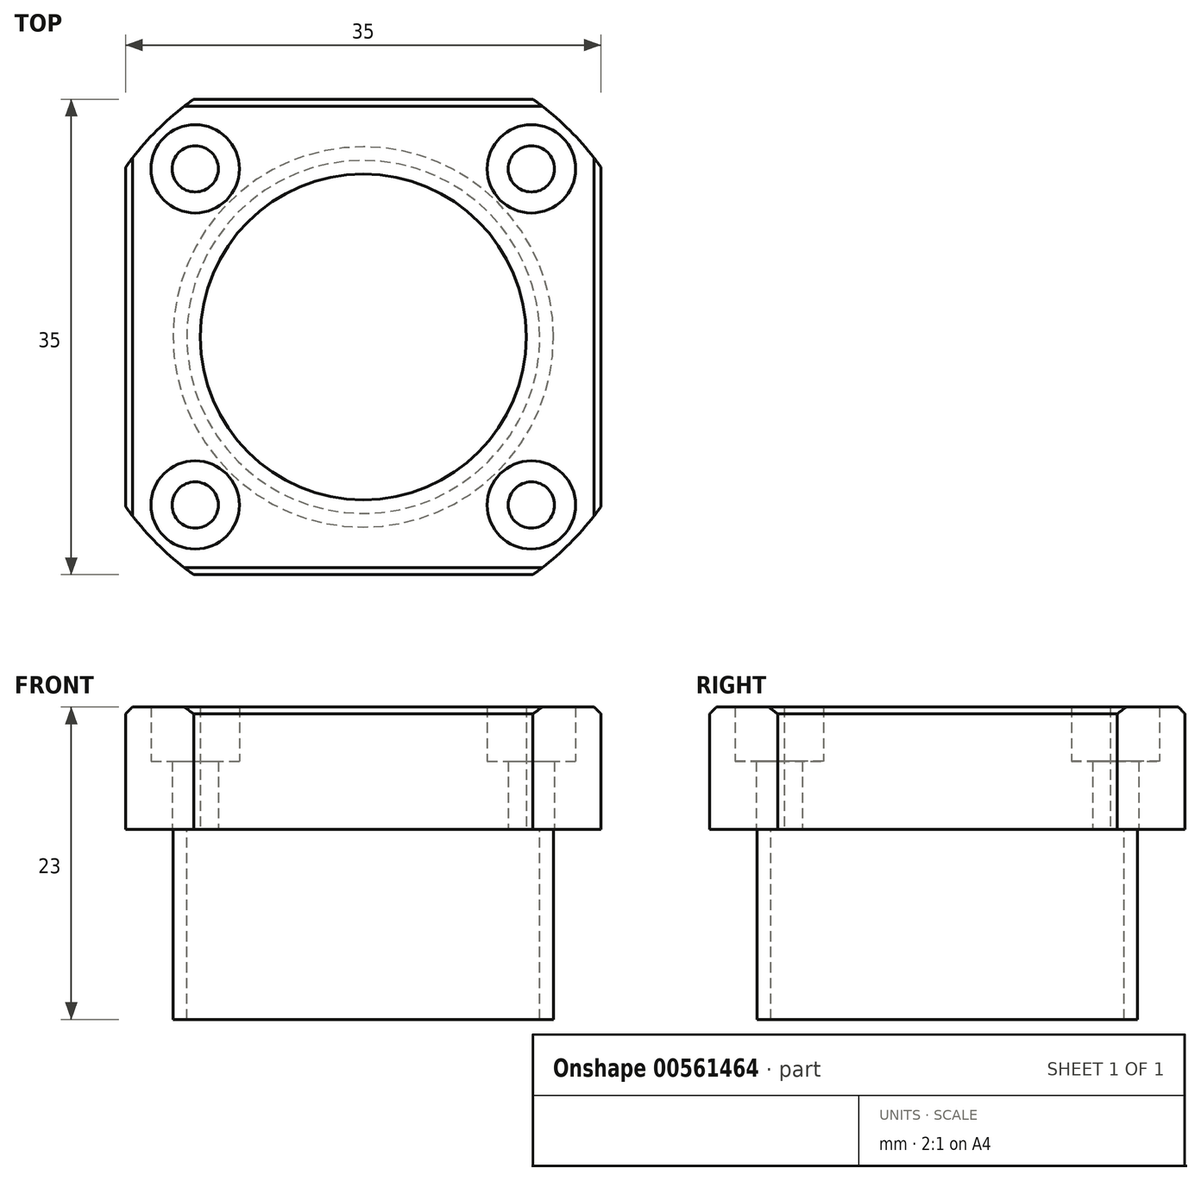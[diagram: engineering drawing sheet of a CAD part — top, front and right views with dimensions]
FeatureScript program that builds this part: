
annotation { "Feature Type Name" : "Feature", "Feature Type Description" : "" }
export const myFeature = defineFeature(function(context is Context, id is Id, definition is map)
    precondition{}
    {
        {
            var Q0;
            Q0=qCreatedBy(makeId("Top.planeOp"),FACE);
            var sketch = newSketch(context, id + "F0", { "sketchPlane" : qUnion([Q0])});
            skLineSegment(sketch, "E0", {"start": v(-17.5, -17.5) * mm, "end": v(17.5, -17.5) * mm});
            skLineSegment(sketch, "E1", {"start": v(17.5, -17.5) * mm, "end": v(17.5, 17.5) * mm});
            skLineSegment(sketch, "E2", {"start": v(17.5, 17.5) * mm, "end": v(-17.5, 17.5) * mm});
            skLineSegment(sketch, "E3", {"start": v(-17.5, 17.5) * mm, "end": v(-17.5, -17.5) * mm});
            skCircle(sketch, "E4", {"center": v(0, 0) * mm, "radius": 17.5 * mm, "construction": true});
            skCircle(sketch, "E5", {"center": v(0, 0) * mm, "radius": 21.5 * mm, "construction": true});
            skLineSegment(sketch, "E6", {"start": v(-17.5, -17.5) * mm, "end": v(17.5, 17.5) * mm, "construction": true});
            skLineSegment(sketch, "E7", {"start": v(-17.5, 17.5) * mm, "end": v(17.5, -17.5) * mm, "construction": true});
            skPoint(sketch, "E8", {"position": v(12.37, -12.37) * mm});
            skPoint(sketch, "E9", {"position": v(12.37, 12.37) * mm});
            skPoint(sketch, "E10", {"position": v(-12.37, 12.37) * mm});
            skPoint(sketch, "E11", {"position": v(-12.37, -12.37) * mm});
            skSolve(sketch);
        }
        {
            var Q0;
            Q0=makeQuery(id+"F0.imprint","IMPRINT",FACE,{"disambiguationData":[TD([[makeQuery(id+"F0.imprint","IMPRINT",EDGE,{"derivedFrom":sQuery(id+"F0.wireOp",EDGE,"E0")}),1.0]])]});
            extrude(context, id + "F1", {"entities" : qUnion([Q0]), "depth" : 9 * mm, "offsetDistance" : 25 * mm});
        }
        {
            var Q0;
            Q0=makeQuery(id+"F1.opExtrude","CAP_FACE",FACE,{"disambiguationData":[OSD([sQuery(id+"F0.wireOp",EDGE,"E0"),sQuery(id+"F0.wireOp",EDGE,"E1"),sQuery(id+"F0.wireOp",EDGE,"E2"),sQuery(id+"F0.wireOp",EDGE,"E3")])],"isStart":true});
            var sketch = newSketch(context, id + "F2", { "sketchPlane" : qUnion([Q0])});
            skCircle(sketch, "E12", {"center": v(0, 0) * mm, "radius": 14 * mm});
            skCircle(sketch, "E13", {"center": v(0, 0) * mm, "radius": 13 * mm});
            skSolve(sketch);
        }
        {
            var Q0;
            Q0=makeQuery(id+"F2.imprint","IMPRINT",FACE,{"disambiguationData":[TD([[makeQuery(id+"F2.imprint","IMPRINT",EDGE,{"derivedFrom":sQuery(id+"F2.wireOp",EDGE,"E12")}),1.0]])]});
            extrude(context, id + "F3", {"entities" : qUnion([Q0]), "operationType" : NewBodyOperationType.ADD, "depth" : 14 * mm, "offsetDistance" : 25 * mm});
        }
        {
            var Q0;
            Q0=makeQuery(id+"F3.boolean.opBoolean","SPLIT",FACE,{"disambiguationData":[TD([makeQuery(id+"F3.opExtrude","SWEPT_FACE",FACE,{"disambiguationData":[OSD([sQuery(id+"F2.wireOp",EDGE,"E13")])]})])],"derivedFrom":makeQuery(id+"F1.opExtrude","CAP_FACE",FACE,{"disambiguationData":[OSD([sQuery(id+"F0.wireOp",EDGE,"E0"),sQuery(id+"F0.wireOp",EDGE,"E1"),sQuery(id+"F0.wireOp",EDGE,"E2"),sQuery(id+"F0.wireOp",EDGE,"E3")])],"isStart":true})});
            extrude(context, id + "F4", {"entities" : qUnion([Q0]), "operationType" : NewBodyOperationType.REMOVE, "endBound" : BoundingType.THROUGH_ALL, "oppositeDirection" : true, "depth" : 25 * mm, "offsetDistance" : 25 * mm});
        }
        {
            var Q0;
            Q0=makeQuery(id+"F1.opExtrude","CAP_FACE",FACE,{"disambiguationData":[OSD([sQuery(id+"F0.wireOp",EDGE,"E0"),sQuery(id+"F0.wireOp",EDGE,"E1"),sQuery(id+"F0.wireOp",EDGE,"E2"),sQuery(id+"F0.wireOp",EDGE,"E3")])],"isStart":false});
            var sketch = newSketch(context, id + "F5", { "sketchPlane" : qUnion([Q0])});
            skPoint(sketch, "E14", {"position": v(-12.37, 12.37) * mm});
            skPoint(sketch, "E15", {"position": v(12.37, 12.37) * mm});
            skPoint(sketch, "E16", {"position": v(12.37, -12.37) * mm});
            skPoint(sketch, "E17", {"position": v(-12.37, -12.37) * mm});
            skCircle(sketch, "E18", {"center": v(0, 0) * mm, "radius": 21.5 * mm});
            skSolve(sketch);
        }
        {
            var Q0;
            Q0=sQuery(id+"F5.wireOp",VERTEX,"E14");
            var Q1;
            Q1=sQuery(id+"F5.wireOp",VERTEX,"E15");
            var Q2;
            Q2=sQuery(id+"F5.wireOp",VERTEX,"E17");
            var Q3;
            Q3=sQuery(id+"F5.wireOp",VERTEX,"E16");
            var Q4;
            Q4=makeQuery(id+"F1.opExtrude","SWEPT_BODY",BODY,{"disambiguationData":[OSD([sQuery(id+"F0.wireOp",EDGE,"E0"),sQuery(id+"F0.wireOp",EDGE,"E1"),sQuery(id+"F0.wireOp",EDGE,"E2"),sQuery(id+"F0.wireOp",EDGE,"E3")])]});
            hole(context, id + "F6", {"style" : HoleStyle.C_BORE, "endStyle" : HoleEndStyle.THROUGH, "holeDiameter" : 3.4 * mm, "cBoreDiameter" : 6.5 * mm, "cBoreDepth" : 4 * mm, "isTappedThrough" : true, "tappedDepth" : 12 * mm, "tapClearance" : 3, "locations" : qUnion([Q0, Q1, Q2, Q3]), "scope" : qUnion([Q4]), "startStyle" : HoleStartStyle.SKETCH});
        }
        {
            var Q0;
            {var subQ0=sQuery(id+"F5.wireOp",EDGE,"E18");var subQ1=makeQuery(id+"F1.opExtrude","CAP_EDGE",EDGE,{"disambiguationData":[OSD([sQuery(id+"F0.wireOp",EDGE,"E2")])],"isStart":false});var subQ2=makeQuery(id+"F5.imprint","INTERSECT",VERTEX,{"disambiguationData":[OD(0.0)],"derivedFrom":[subQ1,subQ0]});Q0=makeQuery(id+"F5.imprint","IMPRINT",FACE,{"disambiguationData":[TD([[makeQuery(id+"F5.imprint","IMPRINT",EDGE,{"disambiguationData":[TD([[subQ2,1.0]])],"derivedFrom":subQ0}),-1.0]])]});}
            var Q1;
            {var subQ0=sQuery(id+"F5.wireOp",EDGE,"E18");var subQ1=makeQuery(id+"F1.opExtrude","CAP_EDGE",EDGE,{"disambiguationData":[OSD([sQuery(id+"F0.wireOp",EDGE,"E2")])],"isStart":false});var subQ2=makeQuery(id+"F5.imprint","INTERSECT",VERTEX,{"disambiguationData":[OD(1.0)],"derivedFrom":[subQ1,subQ0]});Q1=makeQuery(id+"F5.imprint","IMPRINT",FACE,{"disambiguationData":[TD([[makeQuery(id+"F5.imprint","IMPRINT",EDGE,{"disambiguationData":[TD([[subQ2,-1.0]])],"derivedFrom":subQ0}),-1.0]])]});}
            var Q2;
            {var subQ0=sQuery(id+"F5.wireOp",EDGE,"E18");var subQ1=makeQuery(id+"F1.opExtrude","CAP_EDGE",EDGE,{"disambiguationData":[OSD([sQuery(id+"F0.wireOp",EDGE,"E3")])],"isStart":false});var subQ2=makeQuery(id+"F5.imprint","INTERSECT",VERTEX,{"disambiguationData":[OD(1.0)],"derivedFrom":[subQ1,subQ0]});Q2=makeQuery(id+"F5.imprint","IMPRINT",FACE,{"disambiguationData":[TD([[makeQuery(id+"F5.imprint","IMPRINT",EDGE,{"disambiguationData":[TD([[subQ2,-1.0]])],"derivedFrom":subQ0}),-1.0]])]});}
            var Q3;
            {var subQ0=sQuery(id+"F5.wireOp",EDGE,"E18");var subQ1=makeQuery(id+"F1.opExtrude","CAP_EDGE",EDGE,{"disambiguationData":[OSD([sQuery(id+"F0.wireOp",EDGE,"E0")])],"isStart":false});var subQ2=makeQuery(id+"F5.imprint","INTERSECT",VERTEX,{"disambiguationData":[OD(1.0)],"derivedFrom":[subQ1,subQ0]});Q3=makeQuery(id+"F5.imprint","IMPRINT",FACE,{"disambiguationData":[TD([[makeQuery(id+"F5.imprint","IMPRINT",EDGE,{"disambiguationData":[TD([[subQ2,-1.0]])],"derivedFrom":subQ0}),-1.0]])]});}
            extrude(context, id + "F7", {"entities" : qUnion([Q0, Q1, Q2, Q3]), "operationType" : NewBodyOperationType.REMOVE, "endBound" : BoundingType.THROUGH_ALL, "oppositeDirection" : true, "depth" : 25 * mm, "offsetDistance" : 25 * mm});
        }
        {
            var Q0;
            {var subQ0=sQuery(id+"F0.wireOp",EDGE,"E2");var subQ1=sQuery(id+"F0.wireOp",EDGE,"E1");var subQ2=sQuery(id+"F0.wireOp",EDGE,"E3");var subQ3=sQuery(id+"F0.wireOp",EDGE,"E0");Q0=makeQuery(id+"F3.boolean.opBoolean","SPLIT",FACE,{"disambiguationData":[TD([makeQuery(id+"F1.opExtrude","SWEPT_FACE",FACE,{"disambiguationData":[OSD([subQ3])]})])],"derivedFrom":makeQuery(id+"F1.opExtrude","CAP_FACE",FACE,{"disambiguationData":[OSD([subQ3,subQ1,subQ0,subQ2])],"isStart":true})});}
            var sketch = newSketch(context, id + "F8", { "sketchPlane" : qUnion([Q0])});
            skCircle(sketch, "E19", {"center": v(0, 0) * mm, "radius": 12 * mm});
            skSolve(sketch);
        }
        {
            var Q0;
            Q0=makeQuery(id+"F8.imprint","IMPRINT",FACE,{"disambiguationData":[TD([[makeQuery(id+"F8.imprint","IMPRINT",EDGE,{"derivedFrom":sQuery(id+"F8.wireOp",EDGE,"E19")}),-1.0]])]});
            extrude(context, id + "F9", {"entities" : qUnion([Q0]), "operationType" : NewBodyOperationType.ADD, "oppositeDirection" : true, "depth" : 9 * mm, "offsetDistance" : 25 * mm});
        }
        {
            var Q0;
            Q0=makeQuery(id+"F1.opExtrude","CAP_EDGE",EDGE,{"disambiguationData":[OSD([sQuery(id+"F0.wireOp",EDGE,"E0")])],"isStart":false});
            var Q1;
            {var subQ0=sQuery(id+"F5.wireOp",EDGE,"E18");Q1=makeQuery(id+"F7.boolean.opBoolean","COPY",EDGE,{"derivedFrom":makeQuery(id+"F7.opExtrude","CAP_EDGE",EDGE,{"disambiguationData":[OSD([subQ0]),TDD([makeQuery(id+"F5.imprint","IMPRINT",EDGE,{"disambiguationData":[TD([[makeQuery(id+"F5.imprint","INTERSECT",VERTEX,{"disambiguationData":[OD(1.0)],"derivedFrom":[makeQuery(id+"F1.opExtrude","CAP_EDGE",EDGE,{"disambiguationData":[OSD([sQuery(id+"F0.wireOp",EDGE,"E3")])],"isStart":false}),subQ0]}),-1.0]])],"derivedFrom":subQ0})])],"isStart":true})});}
            var Q2;
            Q2=makeQuery(id+"F1.opExtrude","CAP_EDGE",EDGE,{"disambiguationData":[OSD([sQuery(id+"F0.wireOp",EDGE,"E2")])],"isStart":false});
            var Q3;
            {var subQ0=sQuery(id+"F5.wireOp",EDGE,"E18");Q3=makeQuery(id+"F7.boolean.opBoolean","COPY",EDGE,{"derivedFrom":makeQuery(id+"F7.opExtrude","CAP_EDGE",EDGE,{"disambiguationData":[OSD([subQ0]),TDD([makeQuery(id+"F5.imprint","IMPRINT",EDGE,{"disambiguationData":[TD([[makeQuery(id+"F5.imprint","INTERSECT",VERTEX,{"disambiguationData":[OD(0.0)],"derivedFrom":[makeQuery(id+"F1.opExtrude","CAP_EDGE",EDGE,{"disambiguationData":[OSD([sQuery(id+"F0.wireOp",EDGE,"E2")])],"isStart":false}),subQ0]}),1.0]])],"derivedFrom":subQ0})])],"isStart":true})});}
            var Q4;
            Q4=makeQuery(id+"F1.opExtrude","CAP_EDGE",EDGE,{"disambiguationData":[OSD([sQuery(id+"F0.wireOp",EDGE,"E1")])],"isStart":false});
            var Q5;
            {var subQ0=sQuery(id+"F5.wireOp",EDGE,"E18");Q5=makeQuery(id+"F7.boolean.opBoolean","COPY",EDGE,{"derivedFrom":makeQuery(id+"F7.opExtrude","CAP_EDGE",EDGE,{"disambiguationData":[OSD([subQ0]),TDD([makeQuery(id+"F5.imprint","IMPRINT",EDGE,{"disambiguationData":[TD([[makeQuery(id+"F5.imprint","INTERSECT",VERTEX,{"disambiguationData":[OD(1.0)],"derivedFrom":[makeQuery(id+"F1.opExtrude","CAP_EDGE",EDGE,{"disambiguationData":[OSD([sQuery(id+"F0.wireOp",EDGE,"E2")])],"isStart":false}),subQ0]}),-1.0]])],"derivedFrom":subQ0})])],"isStart":true})});}
            var Q6;
            {var subQ0=sQuery(id+"F5.wireOp",EDGE,"E18");Q6=makeQuery(id+"F7.boolean.opBoolean","COPY",EDGE,{"derivedFrom":makeQuery(id+"F7.opExtrude","CAP_EDGE",EDGE,{"disambiguationData":[OSD([subQ0]),TDD([makeQuery(id+"F5.imprint","IMPRINT",EDGE,{"disambiguationData":[TD([[makeQuery(id+"F5.imprint","INTERSECT",VERTEX,{"disambiguationData":[OD(1.0)],"derivedFrom":[makeQuery(id+"F1.opExtrude","CAP_EDGE",EDGE,{"disambiguationData":[OSD([sQuery(id+"F0.wireOp",EDGE,"E0")])],"isStart":false}),subQ0]}),-1.0]])],"derivedFrom":subQ0})])],"isStart":true})});}
            var Q7;
            Q7=makeQuery(id+"F1.opExtrude","CAP_EDGE",EDGE,{"disambiguationData":[OSD([sQuery(id+"F0.wireOp",EDGE,"E3")])],"isStart":false});
            chamfer(context, id + "F10", {"entities" : qUnion([Q0, Q1, Q2, Q3, Q4, Q5, Q6, Q7]), "width" : .5 * mm, "tangentPropagation" : true});
        }
    });
